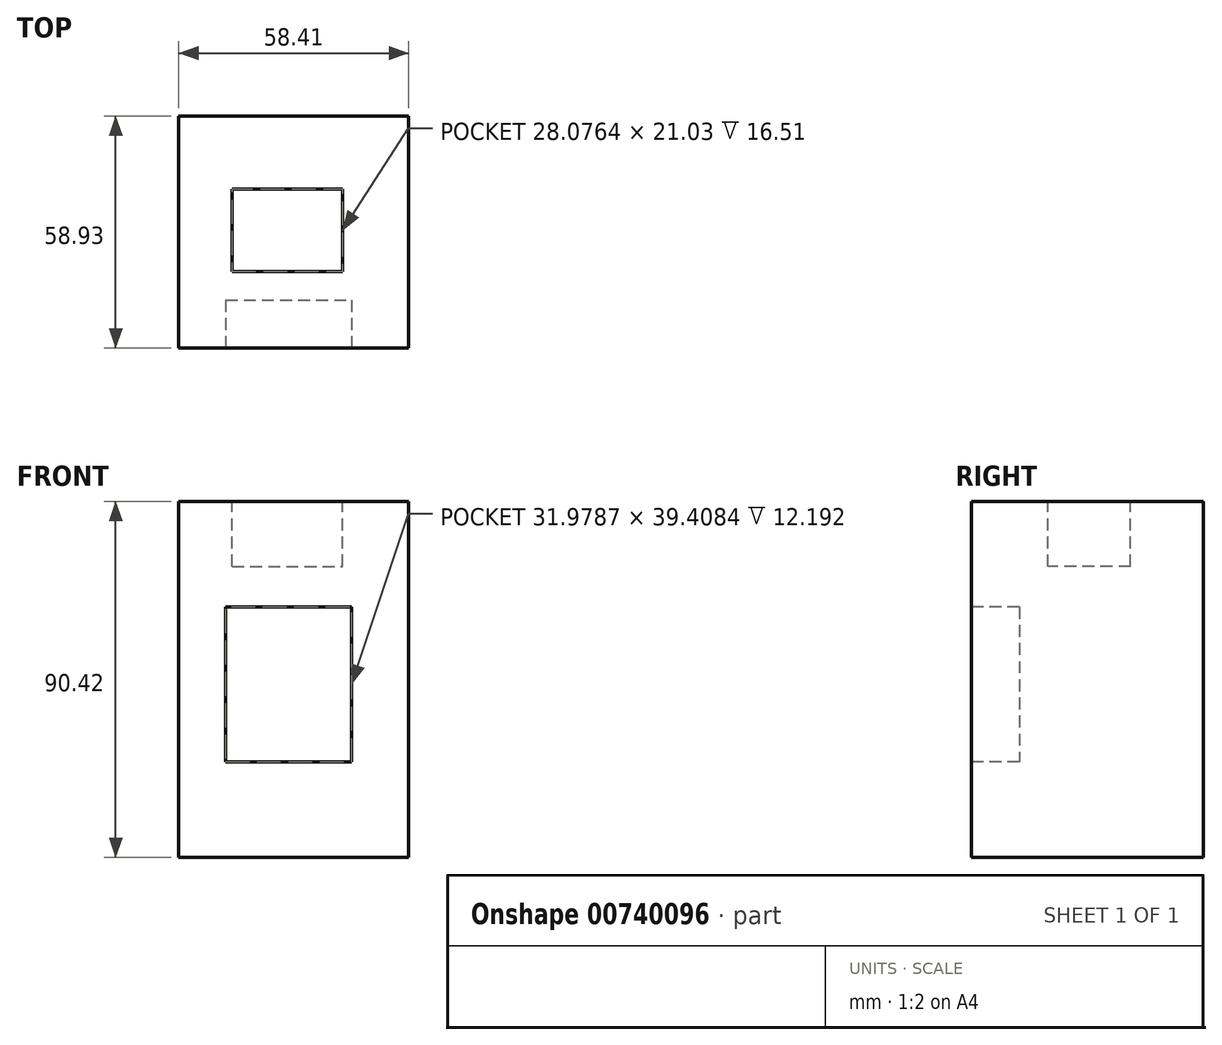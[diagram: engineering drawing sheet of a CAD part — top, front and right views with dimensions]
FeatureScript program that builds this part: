
annotation { "Feature Type Name" : "Feature", "Feature Type Description" : "" }
export const myFeature = defineFeature(function(context is Context, id is Id, definition is map)
    precondition{}
    {
        {
            var Q0;
            Q0=qCreatedBy(makeId("Top.planeOp"),FACE);
            var sketch = newSketch(context, id + "F0", { "sketchPlane" : qUnion([Q0])});
            skLineSegment(sketch, "E0.bottom", {"start": v(-24.92, -19.38) * mm, "end": v(33.49, -19.38) * mm});
            skLineSegment(sketch, "E0.top", {"start": v(-24.92, 39.55) * mm, "end": v(33.49, 39.55) * mm});
            skLineSegment(sketch, "E0.left", {"start": v(-24.92, -19.38) * mm, "end": v(-24.92, 39.55) * mm});
            skLineSegment(sketch, "E0.right", {"start": v(33.49, -19.38) * mm, "end": v(33.49, 39.55) * mm});
            skSolve(sketch);
        }
        {
            var Q0;
            Q0=makeQuery(id+"F0.imprint","IMPRINT",FACE,{"disambiguationData":[TD([[makeQuery(id+"F0.imprint","IMPRINT",EDGE,{"derivedFrom":sQuery(id+"F0.wireOp",EDGE,"E0.bottom")}),1.0]])]});
            extrude(context, id + "F1", {"entities" : qUnion([Q0]), "depth" : 90.42 * mm, "offsetDistance" : 25.4 * mm});
        }
        {
            var Q0;
            Q0=makeQuery(id+"F1.opExtrude","CAP_FACE",FACE,{"disambiguationData":[OSD([sQuery(id+"F0.wireOp",EDGE,"E0.bottom"),sQuery(id+"F0.wireOp",EDGE,"E0.top"),sQuery(id+"F0.wireOp",EDGE,"E0.left"),sQuery(id+"F0.wireOp",EDGE,"E0.right")])],"isStart":false});
            var sketch = newSketch(context, id + "F2", { "sketchPlane" : qUnion([Q0])});
            skLineSegment(sketch, "E1.bottom", {"start": v(-11.37, 21.03) * mm, "end": v(16.7, 21.03) * mm});
            skLineSegment(sketch, "E1.top", {"start": v(-11.37, 0) * mm, "end": v(16.7, 0) * mm});
            skLineSegment(sketch, "E1.left", {"start": v(-11.37, 21.03) * mm, "end": v(-11.37, 0) * mm});
            skLineSegment(sketch, "E1.right", {"start": v(16.7, 21.03) * mm, "end": v(16.7, 0) * mm});
            skSolve(sketch);
        }
        {
            var Q0;
            Q0=makeQuery(id+"F2.imprint","IMPRINT",FACE,{"disambiguationData":[TD([[makeQuery(id+"F2.imprint","IMPRINT",EDGE,{"derivedFrom":sQuery(id+"F2.wireOp",EDGE,"E1.bottom")}),-1.0]])]});
            extrude(context, id + "F3", {"entities" : qUnion([Q0]), "operationType" : NewBodyOperationType.REMOVE, "oppositeDirection" : true, "depth" : 16.5 * mm, "offsetDistance" : 25.4 * mm});
        }
        {
            var Q0;
            Q0=makeQuery(id+"F1.opExtrude","SWEPT_FACE",FACE,{"disambiguationData":[OSD([sQuery(id+"F0.wireOp",EDGE,"E0.bottom")])]});
            var sketch = newSketch(context, id + "F4", { "sketchPlane" : qUnion([Q0])});
            skLineSegment(sketch, "E2.bottom", {"start": v(-13, 63.63) * mm, "end": v(18.98, 63.63) * mm});
            skLineSegment(sketch, "E2.top", {"start": v(-13, 24.23) * mm, "end": v(18.98, 24.23) * mm});
            skLineSegment(sketch, "E2.left", {"start": v(-13, 63.63) * mm, "end": v(-13, 24.23) * mm});
            skLineSegment(sketch, "E2.right", {"start": v(18.98, 63.63) * mm, "end": v(18.98, 24.23) * mm});
            skSolve(sketch);
        }
        {
            var Q0;
            Q0=makeQuery(id+"F4.imprint","IMPRINT",FACE,{"disambiguationData":[TD([[makeQuery(id+"F4.imprint","IMPRINT",EDGE,{"derivedFrom":sQuery(id+"F4.wireOp",EDGE,"E2.bottom")}),-1.0]])]});
            extrude(context, id + "F5", {"entities" : qUnion([Q0]), "operationType" : NewBodyOperationType.REMOVE, "oppositeDirection" : true, "depth" : 12.2 * mm, "offsetDistance" : 25.4 * mm});
        }
    });
